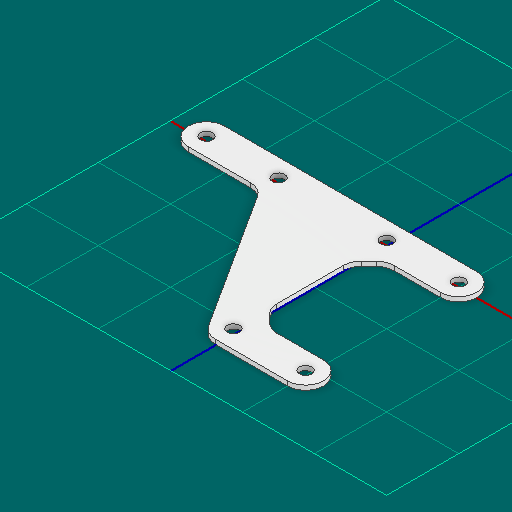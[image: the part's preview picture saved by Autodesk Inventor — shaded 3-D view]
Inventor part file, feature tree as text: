
AUTODESK INVENTOR PART (.ipt)
format: ipt  version: 2025 (Build 290162000, 162)  size: 152,576 bytes
history: native  units: in
note: dims shown in document units (in); Inventor stores cm internally (conversion verified against a paired STEP export)
features: other x5, sketch x1
ambient origin geometry x8: Origin, YZ Plane, XZ Plane, XY Plane, X Axis, Y Axis, Z Axis, Center Point
bodies: Solid1 (feature_tree)
feature tree (6):
  other  "gusset.ipt"
  other  "Blocks"
  other  "main"
  other  "Solid1::gusset.ipt"
  other  "TaggingFeature1"
  sketch  "Sketch1"  dims[d0=0.3937in d1=0.25in]
